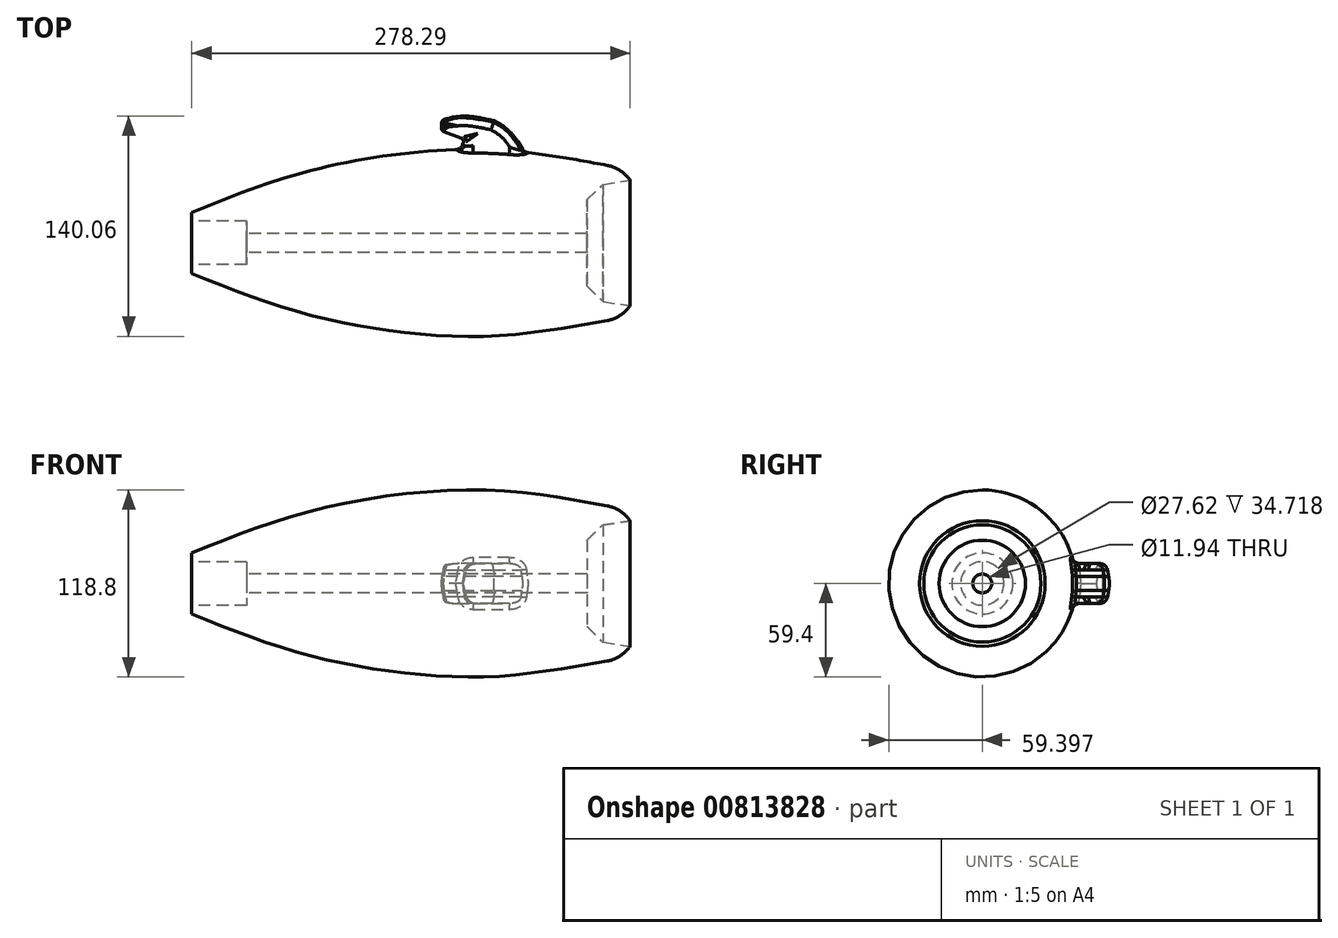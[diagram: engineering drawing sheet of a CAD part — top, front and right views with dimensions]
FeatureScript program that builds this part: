
annotation { "Feature Type Name" : "Feature", "Feature Type Description" : "" }
export const myFeature = defineFeature(function(context is Context, id is Id, definition is map)
    precondition{}
    {
        {
            var Q0;
            Q0=qCreatedBy(makeId("Top.planeOp"),FACE);
            var sketch = newSketch(context, id + "F0", { "sketchPlane" : qUnion([Q0])});
            skFitSpline(sketch, "E0", {"points": [v(-176.76, 10.64) * mm, v(-98.37, 37.9) * mm, v(6.16, 50.58) * mm, v(87.17, 40.5) * mm], "startDerivative": vector(230.75, 93.08) * mm, "endDerivative": vector(242.96, -45.2) * mm});
            skArc(sketch, "E1", {"start": v(87.17, 40.5) * mm, "mid": v(97.57, 35.53) * mm, "end": v(104.07, 26.01) * mm});
            skArc(sketch, "E2", {"start": v(104.07, 26.01) * mm, "mid": v(103.37, 20.99) * mm, "end": v(98.86, 18.66) * mm});
            skLineSegment(sketch, "E3", {"start": v(98.86, 18.66) * mm, "end": v(74.1, 18.66) * mm});
            skLineSegment(sketch, "E4", {"start": v(-176.76, 10.64) * mm, "end": v(-176.76, 5.04) * mm});
            skLineSegment(sketch, "E5", {"start": v(-176.76, 5.04) * mm, "end": v(-142.04, 5.04) * mm});
            skLineSegment(sketch, "E6", {"start": v(-142.04, 5.04) * mm, "end": v(-142.04, -2.8) * mm});
            skLineSegment(sketch, "E7", {"start": v(-142.04, -2.8) * mm, "end": v(74.1, -2.8) * mm});
            skLineSegment(sketch, "E8", {"start": v(74.1, -2.8) * mm, "end": v(74.1, 18.66) * mm});
            skLineSegment(sketch, "E9", {"start": v(74.1, 18.66) * mm, "end": v(84.27, 28.46) * mm});
            skLineSegment(sketch, "E10", {"start": v(84.27, 28.46) * mm, "end": v(101.53, 31.08) * mm});
            skSolve(sketch);
        }
        {
            var Q0;
            Q0=qCreatedBy(makeId("Top.planeOp"),FACE);
            var sketch = newSketch(context, id + "F1", { "sketchPlane" : qUnion([Q0])});
            skLineSegment(sketch, "E11", {"start": v(-98, -8.77) * mm, "end": v(31.54, -8.77) * mm});
            skSolve(sketch);
        }
        {
            var Q0;
            Q0=makeQuery(id+"F0.imprint","IMPRINT",FACE,{"disambiguationData":[TD([[makeQuery(id+"F0.imprint","IMPRINT",EDGE,{"derivedFrom":sQuery(id+"F0.wireOp",EDGE,"E0")}),-1.0]])]});
            var Q1;
            Q1=sQuery(id+"F1.wireOp",EDGE,"E11");
            revolve(context, id + "F2", {"surfaceOperationType" : NewSurfaceOperationType.NEW, "entities" : qUnion([Q0]), "axis" : qUnion([Q1]), "revolveType" : RevolveType.FULL});
        }
        {
            var Q0;
            Q0=qCreatedBy(makeId("Top.planeOp"),FACE);
            var sketch = newSketch(context, id + "F3", { "sketchPlane" : qUnion([Q0])});
            skFitSpline(sketch, "E12", {"points": [v(40.5, 39.01) * mm, v(25.57, 62.16) * mm, v(15.5, 69.25) * mm], "startDerivative": vector(-24.85, 44.9) * mm, "endDerivative": vector(-25.2, 13.5) * mm});
            skFitSpline(sketch, "E13", {"points": [v(15.5, 69.25) * mm, v(-6.53, 72.24) * mm, v(-18.48, 69.25) * mm], "startDerivative": vector(-41.4, 8.7) * mm, "endDerivative": vector(-25.77, -9.6) * mm});
            skLineSegment(sketch, "E14", {"start": v(-18.48, 69.25) * mm, "end": v(-18.48, 62.53) * mm});
            skLineSegment(sketch, "E15", {"start": v(-18.48, 62.53) * mm, "end": v(-3.55, 56.93) * mm});
            skLineSegment(sketch, "E16", {"start": v(-3.55, 56.93) * mm, "end": v(-9, 42.4) * mm});
            skLineSegment(sketch, "E17", {"start": v(-9, 42.4) * mm, "end": v(40.5, 39.01) * mm});
            skSolve(sketch);
        }
        {
            var Q0;
            Q0=makeQuery(id+"F3.imprint","IMPRINT",FACE,{"disambiguationData":[TD([[makeQuery(id+"F3.imprint","IMPRINT",EDGE,{"derivedFrom":sQuery(id+"F3.wireOp",EDGE,"E12")}),1.0]])]});
            extrude(context, id + "F4", {"entities" : qUnion([Q0]), "operationType" : NewBodyOperationType.ADD, "depth" : 25.4 * mm, "offsetDistance" : 25.4 * mm, "hasDraft" : true, "draftAngle" : 10 * degree, "draftPullDirection" : true, "symmetric" : true});
        }
        {
            var Q0;
            Q0=makeQuery(id+"F4.opExtrude","CAP_EDGE",EDGE,{"disambiguationData":[OSD([sQuery(id+"F3.wireOp",EDGE,"E12")])],"isStart":true});
            var Q1;
            Q1=makeQuery(id+"F4.opExtrude","CAP_EDGE",EDGE,{"disambiguationData":[OSD([sQuery(id+"F3.wireOp",EDGE,"E13")])],"isStart":true});
            var Q2;
            Q2=makeQuery(id+"F4.opExtrude","CAP_EDGE",EDGE,{"disambiguationData":[OSD([sQuery(id+"F3.wireOp",EDGE,"E12")])],"isStart":false});
            var Q3;
            Q3=makeQuery(id+"F4.opExtrude","CAP_EDGE",EDGE,{"disambiguationData":[OSD([sQuery(id+"F3.wireOp",EDGE,"E13")])],"isStart":false});
            var Q4;
            Q4=makeQuery(id+"F4.opExtrude","CAP_EDGE",EDGE,{"disambiguationData":[OSD([sQuery(id+"F3.wireOp",EDGE,"E16")])],"isStart":true});
            var Q5;
            Q5=makeQuery(id+"F4.opExtrude","CAP_EDGE",EDGE,{"disambiguationData":[OSD([sQuery(id+"F3.wireOp",EDGE,"E16")])],"isStart":false});
            var Q6;
            Q6=makeQuery(id+"F4.opExtrude","CAP_EDGE",EDGE,{"disambiguationData":[OSD([sQuery(id+"F3.wireOp",EDGE,"E15")])],"isStart":true});
            var Q7;
            Q7=makeQuery(id+"F4.opExtrude","CAP_EDGE",EDGE,{"disambiguationData":[OSD([sQuery(id+"F3.wireOp",EDGE,"E15")])],"isStart":false});
            fillet(context, id + "F5", {"entities" : qUnion([Q0, Q1, Q2, Q3, Q4, Q5, Q6, Q7]), "radius" : 5.08 * mm, "tangentPropagation" : true, "allowEdgeOverflow" : false});
        }
        {
            var Q0;
            {var subQ0=makeQuery(id+"F4.opExtrude","SWEPT_FACE",FACE,{"disambiguationData":[OSD([sQuery(id+"F3.wireOp",EDGE,"E12")])]});Q0=makeQuery(id+"F4.*.booleanUnion.opBoolean","MERGE",EDGE,{"derivedFrom":[makeQuery(id+"F4.*.split.splitOp","SPLIT_SURFACE_INTERSECT",EDGE,{"derivedFrom":[subQ0]}),makeQuery(id+"F4.*.split.splitOp","SPLIT_SURFACE_INTERSECT",EDGE,{"derivedFrom":[subQ0],"isFromBackBody":true})]});}
            var Q1;
            {var subQ0=makeQuery(id+"F4.opExtrude","SWEPT_FACE",FACE,{"disambiguationData":[OSD([sQuery(id+"F3.wireOp",EDGE,"E13")])]});Q1=makeQuery(id+"F4.*.booleanUnion.opBoolean","MERGE",EDGE,{"derivedFrom":[makeQuery(id+"F4.*.split.splitOp","SPLIT_SURFACE_INTERSECT",EDGE,{"derivedFrom":[subQ0]}),makeQuery(id+"F4.*.split.splitOp","SPLIT_SURFACE_INTERSECT",EDGE,{"derivedFrom":[subQ0],"isFromBackBody":true})]});}
            fillet(context, id + "F6", {"entities" : qUnion([Q0, Q1]), "radius" : 25.4 * mm, "tangentPropagation" : true, "allowEdgeOverflow" : false});
        }
        {
            var Q0;
            Q0=makeQuery(id+"F4.boolean.opBoolean","INTERSECT",EDGE,{"derivedFrom":[makeQuery(id+"F2.opRevolve","SWEPT_FACE",FACE,{"disambiguationData":[OSD([sQuery(id+"F0.wireOp",EDGE,"E0")])]}),makeQuery(id+"F4.opExtrude","CAP_FACE",FACE,{"disambiguationData":[OSD([sQuery(id+"F3.wireOp",EDGE,"E12"),sQuery(id+"F3.wireOp",EDGE,"E13"),sQuery(id+"F3.wireOp",EDGE,"E14"),sQuery(id+"F3.wireOp",EDGE,"E15"),sQuery(id+"F3.wireOp",EDGE,"E16"),sQuery(id+"F3.wireOp",EDGE,"E17")])],"isStart":true})]});
            fillet(context, id + "F7", {"entities" : qUnion([Q0]), "radius" : 5.08 * mm, "tangentPropagation" : true, "allowEdgeOverflow" : false});
        }
        {
            var Q0;
            {var subQ0=makeQuery(id+"F4.opExtrude","SWEPT_FACE",FACE,{"disambiguationData":[OSD([sQuery(id+"F3.wireOp",EDGE,"E14")])]});Q0=makeQuery(id+"F4.*.booleanUnion.opBoolean","MERGE",EDGE,{"derivedFrom":[makeQuery(id+"F4.*.split.splitOp","SPLIT_SURFACE_INTERSECT",EDGE,{"derivedFrom":[subQ0]}),makeQuery(id+"F4.*.split.splitOp","SPLIT_SURFACE_INTERSECT",EDGE,{"derivedFrom":[subQ0],"isFromBackBody":true})]});}
            fillet(context, id + "F8", {"entities" : qUnion([Q0]), "radius" : 25.4 * mm, "tangentPropagation" : true, "allowEdgeOverflow" : false});
        }
        {
            var Q0;
            {var subQ0=makeQuery(id+"F4.opExtrude","SWEPT_FACE",FACE,{"disambiguationData":[OSD([sQuery(id+"F3.wireOp",EDGE,"E14")])]});Q0=makeQuery(id+"F8.opFillet","BLEND_EDGE",EDGE,{"blendedFrom":[makeQuery(id+"F4.*.booleanUnion.opBoolean","MERGE",EDGE,{"derivedFrom":[makeQuery(id+"F4.*.split.splitOp","SPLIT_SURFACE_INTERSECT",EDGE,{"derivedFrom":[subQ0]}),makeQuery(id+"F4.*.split.splitOp","SPLIT_SURFACE_INTERSECT",EDGE,{"derivedFrom":[subQ0],"isFromBackBody":true})]}),makeQuery(id+"F6.opFillet","BLEND_FACE",FACE,{"disambiguationData":[OSD([sQuery(id+"F3.wireOp",EDGE,"E13")])]})],"blendedInto":[makeQuery(id+"F6.opFillet","BLEND_FACE",FACE,{"disambiguationData":[OSD([sQuery(id+"F3.wireOp",EDGE,"E13")])]})]});}
            var Q1;
            Q1=makeQuery(id+"F4.*.split.splitOp","SPLIT",EDGE,{"derivedFrom":makeQuery(id+"F4.opExtrude","SWEPT_EDGE",EDGE,{"disambiguationData":[OSD([sQuery(id+"F3.wireOp",EDGE,"E14"),sQuery(id+"F3.wireOp",EDGE,"E15")])]}),"isFromBackBody":true});
            var Q2;
            {var subQ0=makeQuery(id+"F4.opExtrude","SWEPT_FACE",FACE,{"disambiguationData":[OSD([sQuery(id+"F3.wireOp",EDGE,"E14")])]});Q2=makeQuery(id+"F8.opFillet","BLEND_EDGE",EDGE,{"blendedFrom":[makeQuery(id+"F4.*.booleanUnion.opBoolean","MERGE",EDGE,{"derivedFrom":[makeQuery(id+"F4.*.split.splitOp","SPLIT_SURFACE_INTERSECT",EDGE,{"derivedFrom":[subQ0]}),makeQuery(id+"F4.*.split.splitOp","SPLIT_SURFACE_INTERSECT",EDGE,{"derivedFrom":[subQ0],"isFromBackBody":true})]}),makeQuery(id+"F4.*.split.splitOp","SPLIT",FACE,{"derivedFrom":makeQuery(id+"F4.opExtrude","SWEPT_FACE",FACE,{"disambiguationData":[OSD([sQuery(id+"F3.wireOp",EDGE,"E15")])]})})],"blendedInto":[makeQuery(id+"F4.*.split.splitOp","SPLIT",FACE,{"derivedFrom":makeQuery(id+"F4.opExtrude","SWEPT_FACE",FACE,{"disambiguationData":[OSD([sQuery(id+"F3.wireOp",EDGE,"E15")])]})})]});}
            var Q3;
            Q3=makeQuery(id+"F5.opFillet","BLEND_EDGE",EDGE,{"blendedFrom":[makeQuery(id+"F4.opExtrude","CAP_EDGE",EDGE,{"disambiguationData":[OSD([sQuery(id+"F3.wireOp",EDGE,"E13")])],"isStart":false}),makeQuery(id+"F4.opExtrude","CAP_EDGE",EDGE,{"disambiguationData":[OSD([sQuery(id+"F3.wireOp",EDGE,"E15")])],"isStart":false})],"blendedInto":[]});
            var Q4;
            Q4=makeQuery(id+"F5.opFillet","BLEND_EDGE",EDGE,{"blendedFrom":[makeQuery(id+"F4.opExtrude","CAP_EDGE",EDGE,{"disambiguationData":[OSD([sQuery(id+"F3.wireOp",EDGE,"E13")])],"isStart":true}),makeQuery(id+"F4.opExtrude","CAP_EDGE",EDGE,{"disambiguationData":[OSD([sQuery(id+"F3.wireOp",EDGE,"E15")])],"isStart":true})],"blendedInto":[]});
            fillet(context, id + "F9", {"entities" : qUnion([Q0, Q1, Q2, Q3, Q4]), "radius" : 2.03 * mm, "tangentPropagation" : true, "allowEdgeOverflow" : false});
        }
        {
            var Q0;
            Q0=makeQuery(id+"F5.opFillet","BLEND_EDGE",EDGE,{"blendedFrom":[makeQuery(id+"F4.opExtrude","CAP_EDGE",EDGE,{"disambiguationData":[OSD([sQuery(id+"F3.wireOp",EDGE,"E15")])],"isStart":true}),makeQuery(id+"F4.opExtrude","CAP_EDGE",EDGE,{"disambiguationData":[OSD([sQuery(id+"F3.wireOp",EDGE,"E16")])],"isStart":true})],"blendedInto":[]});
            var Q1;
            Q1=makeQuery(id+"F5.opFillet","BLEND_EDGE",EDGE,{"blendedFrom":[makeQuery(id+"F4.opExtrude","CAP_EDGE",EDGE,{"disambiguationData":[OSD([sQuery(id+"F3.wireOp",EDGE,"E15")])],"isStart":false}),makeQuery(id+"F4.opExtrude","CAP_EDGE",EDGE,{"disambiguationData":[OSD([sQuery(id+"F3.wireOp",EDGE,"E16")])],"isStart":false})],"blendedInto":[]});
            fillet(context, id + "F10", {"entities" : qUnion([Q0, Q1]), "radius" : 2.54 * mm, "tangentPropagation" : true, "allowEdgeOverflow" : false});
        }
    });
